# Revit family: MLR-351H-PA
name_source: partatom
category: Mechanical Equipment
revit_build: Autodesk Revit MEP 2012 (Build: 20110309_2315)
units: mm (PartAtom-declared; Revit-internal decimal feet)

## types (1)
- MLR-351H-PA
    Actual Weight = 0
    Body = Galvanized Steel
    Defrost Num Day = 0
    Defrost Termination = Manual
    Defrost Type = Manual
    Description = Plant Growth Chamber
    Door = Galvanized Steel
    Equipment Description = Description
    Equipment Mark = Legend Number
    Evap Temp = -10
    Height = 6' - 0"
    LOAD 1 CLASSIFICATION = Power
    LOAD 1 DEDICATED CIRCUIT REQUIRED = Yes
    LOAD 1 DESCRIPTION = single phase 115V 60Hz
    LOAD 1 ENERGY SETBACK REQUIRED = No
    LOAD 1 GROUND FAULT PROTECTION REQUIRED = No
    LOAD 1 ISOLATED GROUND REQUIRED = No
    LOAD 1 MOUNTING HEIGHT ABOVE FLOOR = 0' - 4"
    LOAD 1 NEUTRAL REQUIRED = Yes
    LOAD 1 PLUG TYPE = NEMA 5-20P
    LOAD 1 POLES = 1
    LOAD 1 VOLTAGE = 115 V
    LOAD 1 WATTAGE = 0 W
    Legend Number = Millimeters
    Length = 2' - 3 1/2"
    Load Mbh = 5118
    Manufacturer = Panasonic
    Model = Panasonic MLR-351H-PA
    Panel = Plastic
    Refrig Charge Lbs = R-404A. 270g
    Supplier = Panasonic Healthcare Company of North America
    Supplier Model = MLR-351H-PA
    URL = http://us.sanyo.com
    Width = 2' - 6"

## geometry (parser evidence)
native form markers: Blend x12, Sweep x3
no freeform markers — native parametric forms only
